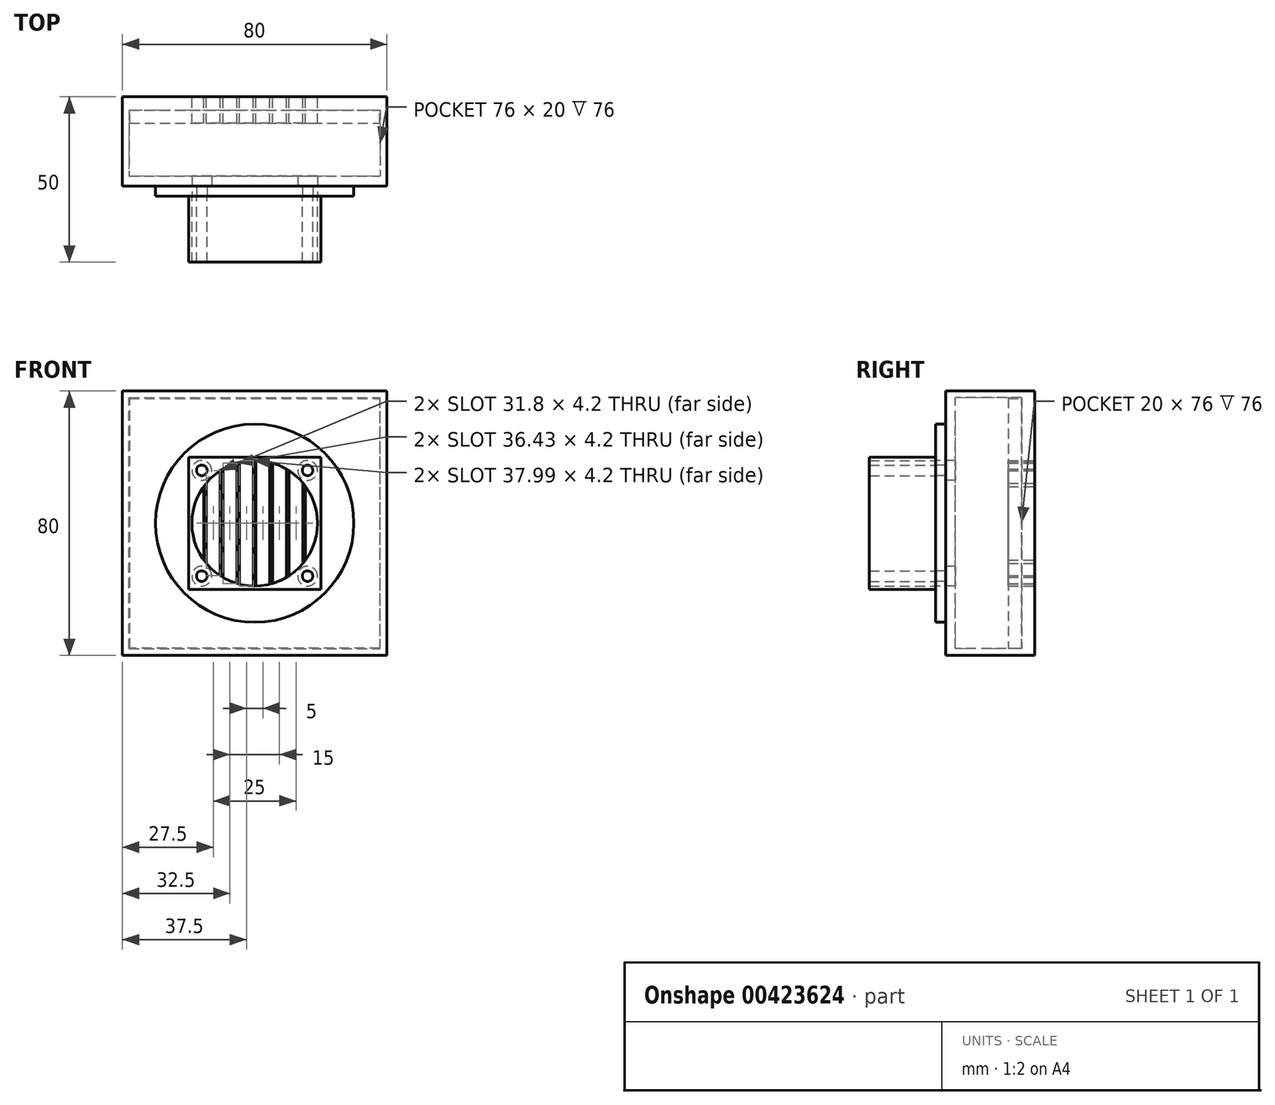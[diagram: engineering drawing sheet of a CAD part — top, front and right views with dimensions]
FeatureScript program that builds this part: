
annotation { "Feature Type Name" : "Feature", "Feature Type Description" : "" }
export const myFeature = defineFeature(function(context is Context, id is Id, definition is map)
    precondition{}
    {
        {
            var Q0;
            Q0=qCreatedBy(makeId("Front.planeOp"),FACE);
            var sketch = newSketch(context, id + "F0", { "sketchPlane" : qUnion([Q0])});
            skLineSegment(sketch, "E0.bottom", {"start": v(20, -20) * mm, "end": v(-20, -20) * mm});
            skLineSegment(sketch, "E0.top", {"start": v(20, 20) * mm, "end": v(-20, 20) * mm});
            skLineSegment(sketch, "E0.left", {"start": v(20, -20) * mm, "end": v(20, 20) * mm});
            skLineSegment(sketch, "E0.right", {"start": v(-20, -20) * mm, "end": v(-20, 20) * mm});
            skPoint(sketch, "E0.middle", {"position": v(0, 0) * mm});
            skCircle(sketch, "E1", {"center": v(0, 0) * mm, "radius": 19 * mm});
            skCircle(sketch, "E2", {"center": v(-16, 16) * mm, "radius": 1.6 * mm});
            skCircle(sketch, "E3.MirrorC", {"center": v(16, 16) * mm, "radius": 1.6 * mm});
            skCircle(sketch, "E4.MirrorC", {"center": v(-16, -16) * mm, "radius": 1.6 * mm});
            skCircle(sketch, "E5.MirrorC", {"center": v(16, -16) * mm, "radius": 1.6 * mm});
            skSolve(sketch);
        }
        {
            var Q0;
            Q0=makeQuery(id+"F0.imprint","IMPRINT",FACE,{"disambiguationData":[TD([[makeQuery(id+"F0.imprint","IMPRINT",EDGE,{"derivedFrom":sQuery(id+"F0.wireOp",EDGE,"E0.bottom")}),-1.0]])]});
            extrude(context, id + "F1", {"entities" : qUnion([Q0]), "depth" : 20 * mm});
        }
        {
            var Q0;
            Q0=makeQuery(id+"F1.opExtrude","CAP_FACE",FACE,{"disambiguationData":[OSD([sQuery(id+"F0.wireOp",EDGE,"E0.bottom"),sQuery(id+"F0.wireOp",EDGE,"E0.top"),sQuery(id+"F0.wireOp",EDGE,"E0.left"),sQuery(id+"F0.wireOp",EDGE,"E0.right"),sQuery(id+"F0.wireOp",EDGE,"E1"),sQuery(id+"F0.wireOp",EDGE,"E2"),sQuery(id+"F0.wireOp",EDGE,"E3.MirrorC"),sQuery(id+"F0.wireOp",EDGE,"E4.MirrorC"),sQuery(id+"F0.wireOp",EDGE,"E5.MirrorC")])],"isStart":true});
            var sketch = newSketch(context, id + "F2", { "sketchPlane" : qUnion([Q0])});
            skCircle(sketch, "E6", {"center": v(0, 0) * mm, "radius": 30 * mm});
            skCircle(sketch, "E7.0", {"center": v(0, 0) * mm, "radius": 19 * mm});
            skSolve(sketch);
        }
        {
            var Q0;
            Q0=makeQuery(id+"F2.imprint","IMPRINT",FACE,{"disambiguationData":[TD([[makeQuery(id+"F2.imprint","IMPRINT",EDGE,{"derivedFrom":sQuery(id+"F2.wireOp",EDGE,"E6")}),1.0]])]});
            var Q1;
            Q1=makeQuery(id+"F2.imprint","IMPRINT",FACE,{"disambiguationData":[TD([[makeQuery(id+"F2.imprint","IMPRINT",EDGE,{"derivedFrom":sQuery(id+"F2.wireOp",EDGE,"E7.0")}),1.0]])]});
            extrude(context, id + "F3", {"entities" : qUnion([Q0, Q1]), "depth" : 3 * mm});
        }
        {
            var Q0;
            Q0=makeQuery(id+"F3.opExtrude","CAP_FACE",FACE,{"disambiguationData":[OSD([sQuery(id+"F0.wireOp",EDGE,"E2"),sQuery(id+"F0.wireOp",EDGE,"E3.MirrorC"),sQuery(id+"F0.wireOp",EDGE,"E4.MirrorC"),sQuery(id+"F0.wireOp",EDGE,"E5.MirrorC"),sQuery(id+"F2.wireOp",EDGE,"E6"),sQuery(id+"F2.wireOp",EDGE,"E7.0")])],"isStart":false});
            var sketch = newSketch(context, id + "F4", { "sketchPlane" : qUnion([Q0])});
            skLineSegment(sketch, "E8.bottom", {"start": v(40, -40) * mm, "end": v(-40, -40) * mm});
            skLineSegment(sketch, "E8.top", {"start": v(40, 40) * mm, "end": v(-40, 40) * mm});
            skLineSegment(sketch, "E8.left", {"start": v(40, -40) * mm, "end": v(40, 40) * mm});
            skLineSegment(sketch, "E8.right", {"start": v(-40, -40) * mm, "end": v(-40, 40) * mm});
            skCircle(sketch, "E9", {"center": v(-16, 16) * mm, "radius": 3 * mm});
            skCircle(sketch, "E10", {"center": v(16, 16) * mm, "radius": 3 * mm});
            skCircle(sketch, "E11", {"center": v(16, -16) * mm, "radius": 3 * mm});
            skCircle(sketch, "E12", {"center": v(-16, -16) * mm, "radius": 3 * mm});
            skCircle(sketch, "E13.0", {"center": v(0, 0) * mm, "radius": 19 * mm});
            skSolve(sketch);
        }
        {
            var Q0;
            Q0=makeQuery(id+"F4.imprint","IMPRINT",FACE,{"disambiguationData":[TD([[makeQuery(id+"F4.imprint","IMPRINT",EDGE,{"derivedFrom":sQuery(id+"F4.wireOp",EDGE,"gEd9JgBY-sdqf-Gc1U-44YO-QilP8WneGw9F")}),-1.0]])]});
            var Q1;
            {var subQ0=sQuery(id+"F4.wireOp",EDGE,"E8.right");var subQ1=sQuery(id+"F4.wireOp",EDGE,"E8.bottom");var subQ2=makeQuery(id+"F4.imprint","INTERSECT",VERTEX,{"derivedFrom":[subQ1,subQ0]});Q1=makeQuery(id+"F4.imprint","IMPRINT",FACE,{"disambiguationData":[TD([[makeQuery(id+"F4.imprint","IMPRINT",EDGE,{"disambiguationData":[TD([[subQ2,1.0]])],"derivedFrom":subQ1}),-1.0]])]});}
            var Q2;
            {var subQ0=sQuery(id+"F4.wireOp",EDGE,"E8.left");var subQ1=sQuery(id+"F4.wireOp",EDGE,"E8.bottom");var subQ2=makeQuery(id+"F4.imprint","INTERSECT",VERTEX,{"derivedFrom":[subQ1,subQ0]});Q2=makeQuery(id+"F4.imprint","IMPRINT",FACE,{"disambiguationData":[TD([[makeQuery(id+"F4.imprint","IMPRINT",EDGE,{"disambiguationData":[TD([[subQ2,-1.0]])],"derivedFrom":subQ1}),-1.0]])]});}
            var Q3;
            {var subQ0=sQuery(id+"F4.wireOp",EDGE,"E8.left");var subQ1=sQuery(id+"F4.wireOp",EDGE,"E8.top");var subQ2=makeQuery(id+"F4.imprint","INTERSECT",VERTEX,{"derivedFrom":[subQ1,subQ0]});Q3=makeQuery(id+"F4.imprint","IMPRINT",FACE,{"disambiguationData":[TD([[makeQuery(id+"F4.imprint","IMPRINT",EDGE,{"disambiguationData":[TD([[subQ2,-1.0]])],"derivedFrom":subQ1}),1.0]])]});}
            var Q4;
            {var subQ0=sQuery(id+"F4.wireOp",EDGE,"E8.right");var subQ1=sQuery(id+"F4.wireOp",EDGE,"E8.top");var subQ2=makeQuery(id+"F4.imprint","INTERSECT",VERTEX,{"derivedFrom":[subQ1,subQ0]});Q4=makeQuery(id+"F4.imprint","IMPRINT",FACE,{"disambiguationData":[TD([[makeQuery(id+"F4.imprint","IMPRINT",EDGE,{"disambiguationData":[TD([[subQ2,1.0]])],"derivedFrom":subQ1}),1.0]])]});}
            var Q5;
            Q5=makeQuery(id+"F4.imprint","IMPRINT",FACE,{"disambiguationData":[TD([[makeQuery(id+"F4.imprint","IMPRINT",EDGE,{"derivedFrom":sQuery(id+"F4.wireOp",EDGE,"E9")}),-1.0]])]});
            extrude(context, id + "F5", {"entities" : qUnion([Q0, Q1, Q2, Q3, Q4, Q5]), "operationType" : NewBodyOperationType.ADD, "depth" : 3 * mm});
        }
        {
            var Q0;
            Q0=makeQuery(id+"F5.opExtrude","CAP_FACE",FACE,{"disambiguationData":[OSD([sQuery(id+"F4.wireOp",EDGE,"E8.bottom"),sQuery(id+"F4.wireOp",EDGE,"E8.top"),sQuery(id+"F4.wireOp",EDGE,"E8.left"),sQuery(id+"F4.wireOp",EDGE,"E8.right"),sQuery(id+"F4.wireOp",EDGE,"gEd9JgBY-sdqf-Gc1U-44YO-QilP8WneGw9F"),sQuery(id+"F4.wireOp",EDGE,"ywT1FPnq-o6qU-tjFV-ppvE-6aCUMW5xF5HS"),sQuery(id+"F4.wireOp",EDGE,"A4RIJUq3-oKKo-Abm0-WiMj-i7iOZli3vFoU"),sQuery(id+"F4.wireOp",EDGE,"nQKl4K2k-JCYA-71Lq-16MN-hBtVShvXbRyy"),sQuery(id+"F4.wireOp",EDGE,"Mxee1EwI-FkuX-YyNC-LaR6-tGNms4gIIVxV"),sQuery(id+"F4.wireOp",EDGE,"685b2f9b-b845-48d3-9249-d7e1dc3f7470.trimOffspring"),sQuery(id+"F4.wireOp",EDGE,"5944e53f-1123-4851-8d29-a6545013498c.trimOffspring"),sQuery(id+"F4.wireOp",EDGE,"1fc4f888-6afe-459b-bbca-8157845f3e42.trimOffspring")])],"isStart":false});
            var sketch = newSketch(context, id + "F6", { "sketchPlane" : qUnion([Q0])});
            skLineSegment(sketch, "E14.0", {"start": v(38, 38) * mm, "end": v(-38, 38) * mm});
            skLineSegment(sketch, "E14.1", {"start": v(38, -38) * mm, "end": v(38, 38) * mm});
            skLineSegment(sketch, "E14.2", {"start": v(38, -38) * mm, "end": v(-38, -38) * mm});
            skLineSegment(sketch, "E14.3", {"start": v(-38, -38) * mm, "end": v(-38, 38) * mm});
            skLineSegment(sketch, "E15.0", {"start": v(37.8, 37.8) * mm, "end": v(-37.8, 37.8) * mm});
            skLineSegment(sketch, "E15.1", {"start": v(37.8, -37.8) * mm, "end": v(37.8, 37.8) * mm});
            skLineSegment(sketch, "E15.2", {"start": v(37.8, -37.8) * mm, "end": v(-37.8, -37.8) * mm});
            skLineSegment(sketch, "E15.3", {"start": v(-37.8, -37.8) * mm, "end": v(-37.8, 37.8) * mm});
            skSolve(sketch);
        }
        {
            var Q0;
            Q0=makeQuery(id+"F6.imprint","IMPRINT",FACE,{"disambiguationData":[TD([[makeQuery(id+"F6.imprint","IMPRINT",EDGE,{"derivedFrom":sQuery(id+"F6.wireOp",EDGE,"E14.0")}),-1.0]])]});
            extrude(context, id + "F7", {"entities" : qUnion([Q0]), "operationType" : NewBodyOperationType.ADD, "depth" : 20 * mm});
        }
        {
            var Q0;
            Q0=makeQuery(id+"F7.opExtrude","CAP_FACE",FACE,{"disambiguationData":[OSD([sQuery(id+"F4.wireOp",EDGE,"E8.bottom"),sQuery(id+"F4.wireOp",EDGE,"E8.top"),sQuery(id+"F4.wireOp",EDGE,"E8.left"),sQuery(id+"F4.wireOp",EDGE,"E8.right"),sQuery(id+"F6.wireOp",EDGE,"E14.0"),sQuery(id+"F6.wireOp",EDGE,"E14.1"),sQuery(id+"F6.wireOp",EDGE,"E14.2"),sQuery(id+"F6.wireOp",EDGE,"E14.3")])],"isStart":false});
            var sketch = newSketch(context, id + "F8", { "sketchPlane" : qUnion([Q0])});
            skLineSegment(sketch, "E16.0.0", {"start": v(-37.8, 37.8) * mm, "end": v(-37.8, -37.8) * mm});
            skLineSegment(sketch, "E16.0.1", {"start": v(-37.8, -37.8) * mm, "end": v(37.8, -37.8) * mm});
            skLineSegment(sketch, "E16.0.2", {"start": v(37.8, -37.8) * mm, "end": v(37.8, 37.8) * mm});
            skLineSegment(sketch, "E16.0.3", {"start": v(37.8, 37.8) * mm, "end": v(-37.8, 37.8) * mm});
            skCircle(sketch, "E17.0", {"center": v(0, 0) * mm, "radius": 19 * mm});
            skLineSegment(sketch, "E18.0", {"start": v(-40, -40) * mm, "end": v(-40, 40) * mm});
            skLineSegment(sketch, "E19.0", {"start": v(40, 40) * mm, "end": v(-40, 40) * mm});
            skLineSegment(sketch, "E20.0", {"start": v(40, -40) * mm, "end": v(40, 40) * mm});
            skLineSegment(sketch, "E21.0", {"start": v(40, -40) * mm, "end": v(-40, -40) * mm});
            skLineSegment(sketch, "E22.0", {"start": v(38, -38) * mm, "end": v(-38, -38) * mm});
            skLineSegment(sketch, "E23.0", {"start": v(-38, -38) * mm, "end": v(-38, 38) * mm});
            skLineSegment(sketch, "E24.0", {"start": v(38, -38) * mm, "end": v(38, 38) * mm});
            skLineSegment(sketch, "E25.0", {"start": v(38, 38) * mm, "end": v(-38, 38) * mm});
            skLineSegment(sketch, "E26", {"start": v(-0.4, 19) * mm, "end": v(-0.4, -19) * mm});
            skLineSegment(sketch, "E27", {"start": v(0.4, -19) * mm, "end": v(0.4, 19) * mm});
            skLineSegment(sketch, "E28.1.0.0", {"start": v(4.6, 18.43) * mm, "end": v(4.6, -18.43) * mm});
            skLineSegment(sketch, "E28.1.0.1", {"start": v(5.4, -18.22) * mm, "end": v(5.4, 18.22) * mm});
            skLineSegment(sketch, "E28.2.0.0", {"start": v(9.6, 16.4) * mm, "end": v(9.6, -16.4) * mm});
            skLineSegment(sketch, "E28.2.0.1", {"start": v(10.4, -15.9) * mm, "end": v(10.4, 15.9) * mm});
            skLineSegment(sketch, "E28.3.0.0", {"start": v(14.6, 12.16) * mm, "end": v(14.6, -12.16) * mm});
            skLineSegment(sketch, "E28.3.0.1", {"start": v(15.4, -11.13) * mm, "end": v(15.4, 11.13) * mm});
            skLineSegment(sketch, "E28.direction1", {"start": v(-0.4, -37.8) * mm, "end": v(4.6, -37.8) * mm, "construction": true});
            skPoint(sketch, "E29", {"position": v(0.4, 19) * mm});
            skPoint(sketch, "E30", {"position": v(4.6, 18.43) * mm});
            skPoint(sketch, "E31", {"position": v(5.4, 18.22) * mm});
            skPoint(sketch, "E32", {"position": v(9.6, 16.4) * mm});
            skPoint(sketch, "E33", {"position": v(10.4, 15.9) * mm});
            skPoint(sketch, "E34", {"position": v(14.6, 12.16) * mm});
            skPoint(sketch, "E35", {"position": v(15.4, 11.13) * mm});
            skPoint(sketch, "E36", {"position": v(14.6, -12.16) * mm});
            skPoint(sketch, "E37", {"position": v(15.4, -11.13) * mm});
            skPoint(sketch, "E38", {"position": v(10.4, -15.9) * mm});
            skPoint(sketch, "E39", {"position": v(9.6, -16.4) * mm});
            skPoint(sketch, "E40", {"position": v(5.4, -18.22) * mm});
            skPoint(sketch, "E41", {"position": v(4.6, -18.43) * mm});
            skPoint(sketch, "E42", {"position": v(0.4, -19) * mm});
            skPoint(sketch, "E43.orphan", {"position": v(-0.4, 37.8) * mm});
            skPoint(sketch, "E44.orphan", {"position": v(0.4, 37.8) * mm});
            skPoint(sketch, "E45.orphan", {"position": v(4.6, 37.8) * mm});
            skPoint(sketch, "E46.orphan", {"position": v(5.4, 37.8) * mm});
            skPoint(sketch, "E47.orphan", {"position": v(10.4, 37.8) * mm});
            skPoint(sketch, "E48.orphan", {"position": v(9.6, 37.8) * mm});
            skPoint(sketch, "E49.orphan", {"position": v(14.6, 37.8) * mm});
            skPoint(sketch, "E50.orphan", {"position": v(15.4, 37.8) * mm});
            skPoint(sketch, "E51.orphan", {"position": v(0.4, -37.8) * mm});
            skPoint(sketch, "E52.orphan", {"position": v(5.4, -37.8) * mm});
            skPoint(sketch, "E53.orphan", {"position": v(9.6, -37.8) * mm});
            skPoint(sketch, "E54.orphan", {"position": v(10.4, -37.8) * mm});
            skPoint(sketch, "E55.orphan", {"position": v(14.6, -37.8) * mm});
            skPoint(sketch, "E56.orphan", {"position": v(15.4, -37.8) * mm});
            skLineSegment(sketch, "E57.MirrorCS", {"start": v(-4.6, 18.43) * mm, "end": v(-4.6, -18.43) * mm});
            skLineSegment(sketch, "E58.MirrorCS", {"start": v(-5.4, -18.22) * mm, "end": v(-5.4, 18.22) * mm});
            skLineSegment(sketch, "E59.MirrorCS", {"start": v(-9.6, 16.4) * mm, "end": v(-9.6, -16.4) * mm});
            skLineSegment(sketch, "E60.MirrorCS", {"start": v(-10.4, -15.9) * mm, "end": v(-10.4, 15.9) * mm});
            skLineSegment(sketch, "E61.MirrorCS", {"start": v(-14.6, 12.16) * mm, "end": v(-14.6, -12.16) * mm});
            skLineSegment(sketch, "E62.MirrorCS", {"start": v(-15.4, -11.13) * mm, "end": v(-15.4, 11.13) * mm});
            skSolve(sketch);
        }
        {
            var Q0;
            Q0=makeQuery(id+"F8.imprint","IMPRINT",FACE,{"disambiguationData":[TD([[makeQuery(id+"F8.imprint","IMPRINT",EDGE,{"derivedFrom":sQuery(id+"F8.wireOp",EDGE,"E16.0.0")}),1.0]])]});
            var Q1;
            {var subQ0=sQuery(id+"F8.wireOp",EDGE,"E61.MirrorCS");Q1=makeQuery(id+"F8.imprint","IMPRINT",FACE,{"disambiguationData":[TD([[makeQuery(id+"F8.imprint","IMPRINT",EDGE,{"derivedFrom":subQ0}),-1.0]])]});}
            var Q2;
            {var subQ0=sQuery(id+"F8.wireOp",EDGE,"E59.MirrorCS");Q2=makeQuery(id+"F8.imprint","IMPRINT",FACE,{"disambiguationData":[TD([[makeQuery(id+"F8.imprint","IMPRINT",EDGE,{"derivedFrom":subQ0}),-1.0]])]});}
            var Q3;
            {var subQ0=sQuery(id+"F8.wireOp",EDGE,"E57.MirrorCS");Q3=makeQuery(id+"F8.imprint","IMPRINT",FACE,{"disambiguationData":[TD([[makeQuery(id+"F8.imprint","IMPRINT",EDGE,{"derivedFrom":subQ0}),-1.0]])]});}
            var Q4;
            {var subQ0=sQuery(id+"F8.wireOp",EDGE,"E26");Q4=makeQuery(id+"F8.imprint","IMPRINT",FACE,{"disambiguationData":[TD([[makeQuery(id+"F8.imprint","IMPRINT",EDGE,{"derivedFrom":subQ0}),1.0]])]});}
            var Q5;
            {var subQ0=sQuery(id+"F8.wireOp",EDGE,"E28.1.0.0");Q5=makeQuery(id+"F8.imprint","IMPRINT",FACE,{"disambiguationData":[TD([[makeQuery(id+"F8.imprint","IMPRINT",EDGE,{"derivedFrom":subQ0}),1.0]])]});}
            var Q6;
            {var subQ0=sQuery(id+"F8.wireOp",EDGE,"E28.2.0.0");Q6=makeQuery(id+"F8.imprint","IMPRINT",FACE,{"disambiguationData":[TD([[makeQuery(id+"F8.imprint","IMPRINT",EDGE,{"derivedFrom":subQ0}),1.0]])]});}
            var Q7;
            {var subQ0=sQuery(id+"F8.wireOp",EDGE,"E28.3.0.0");Q7=makeQuery(id+"F8.imprint","IMPRINT",FACE,{"disambiguationData":[TD([[makeQuery(id+"F8.imprint","IMPRINT",EDGE,{"derivedFrom":subQ0}),1.0]])]});}
            extrude(context, id + "F9", {"entities" : qUnion([Q0, Q1, Q2, Q3, Q4, Q5, Q6, Q7]), "oppositeDirection" : true, "depth" : 4 * mm});
        }
        {
            var Q0;
            Q0 = qSketchRegion(id + "F8", true);
            var Q1;
            Q1=makeQuery(id+"F8.imprint","IMPRINT",FACE,{"disambiguationData":[TD([[makeQuery(id+"F8.imprint","IMPRINT",EDGE,{"derivedFrom":sQuery(id+"F8.wireOp",EDGE,"E16.0.0")}),-1.0]])]});
            var Q2;
            Q2=makeQuery(id+"F8.imprint","IMPRINT",FACE,{"disambiguationData":[TD([[makeQuery(id+"F8.imprint","IMPRINT",EDGE,{"derivedFrom":sQuery(id+"F8.wireOp",EDGE,"E16.0.0")}),1.0]])]});
            var Q3;
            {var subQ0=sQuery(id+"F8.wireOp",EDGE,"E59.MirrorCS");Q3=makeQuery(id+"F8.imprint","IMPRINT",FACE,{"disambiguationData":[TD([[makeQuery(id+"F8.imprint","IMPRINT",EDGE,{"derivedFrom":subQ0}),-1.0]])]});}
            var Q4;
            {var subQ0=sQuery(id+"F8.wireOp",EDGE,"E61.MirrorCS");Q4=makeQuery(id+"F8.imprint","IMPRINT",FACE,{"disambiguationData":[TD([[makeQuery(id+"F8.imprint","IMPRINT",EDGE,{"derivedFrom":subQ0}),-1.0]])]});}
            var Q5;
            {var subQ0=sQuery(id+"F8.wireOp",EDGE,"E57.MirrorCS");Q5=makeQuery(id+"F8.imprint","IMPRINT",FACE,{"disambiguationData":[TD([[makeQuery(id+"F8.imprint","IMPRINT",EDGE,{"derivedFrom":subQ0}),-1.0]])]});}
            var Q6;
            {var subQ0=sQuery(id+"F8.wireOp",EDGE,"E26");Q6=makeQuery(id+"F8.imprint","IMPRINT",FACE,{"disambiguationData":[TD([[makeQuery(id+"F8.imprint","IMPRINT",EDGE,{"derivedFrom":subQ0}),1.0]])]});}
            var Q7;
            {var subQ0=sQuery(id+"F8.wireOp",EDGE,"E28.1.0.0");Q7=makeQuery(id+"F8.imprint","IMPRINT",FACE,{"disambiguationData":[TD([[makeQuery(id+"F8.imprint","IMPRINT",EDGE,{"derivedFrom":subQ0}),1.0]])]});}
            var Q8;
            {var subQ0=sQuery(id+"F8.wireOp",EDGE,"E28.2.0.0");Q8=makeQuery(id+"F8.imprint","IMPRINT",FACE,{"disambiguationData":[TD([[makeQuery(id+"F8.imprint","IMPRINT",EDGE,{"derivedFrom":subQ0}),1.0]])]});}
            var Q9;
            {var subQ0=sQuery(id+"F8.wireOp",EDGE,"E28.3.0.0");Q9=makeQuery(id+"F8.imprint","IMPRINT",FACE,{"disambiguationData":[TD([[makeQuery(id+"F8.imprint","IMPRINT",EDGE,{"derivedFrom":subQ0}),1.0]])]});}
            extrude(context, id + "F10", {"entities" : qUnion([Q0, Q1, Q2, Q3, Q4, Q5, Q6, Q7, Q8, Q9]), "operationType" : NewBodyOperationType.ADD, "depth" : 4 * mm});
        }
    });
